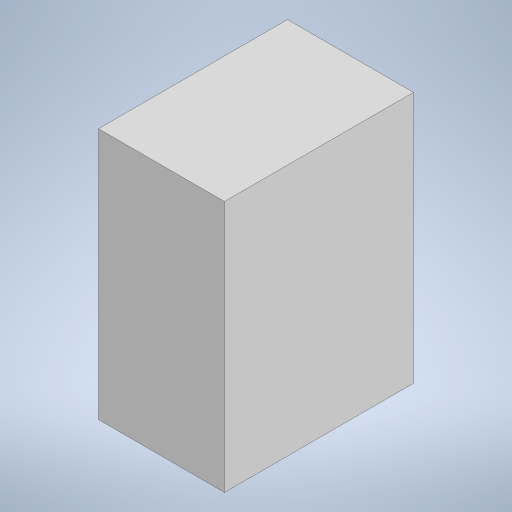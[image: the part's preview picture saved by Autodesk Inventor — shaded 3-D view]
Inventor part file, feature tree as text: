
AUTODESK INVENTOR PART (.ipt)
format: ipt  version: 2023 (Build 270158000, 158)  size: 224,768 bytes
history: native  units: in
note: dims shown in document units (in); Inventor stores cm internally (conversion verified against a paired STEP export)
features: extrude x3, sketch x2
ambient origin geometry x8: Origin, YZ Plane, XZ Plane, XY Plane, X Axis, Y Axis, Z Axis, Center Point
bodies: Solid1 (feature_tree)
feature tree (5):
  sketch  "Sketch1"  dims[d0=0.5in d1=1.0in]
  extrude  "Extrusion1"  Depth=1.0in
  extrude  "Extrusion4"  Depth=0.5in
  extrude  "Extrusion5"  Depth=0.5in
  sketch  "Sketch3"  dims[d2=1.5in d3=0.5in d4=0.5in d5=2.0in d6=0.0in d21=1.75in d22=0.0in d23=0.125in d24=0.125in d25=1.0in d26=0.5in d27=1.0in d28=0.0in]
